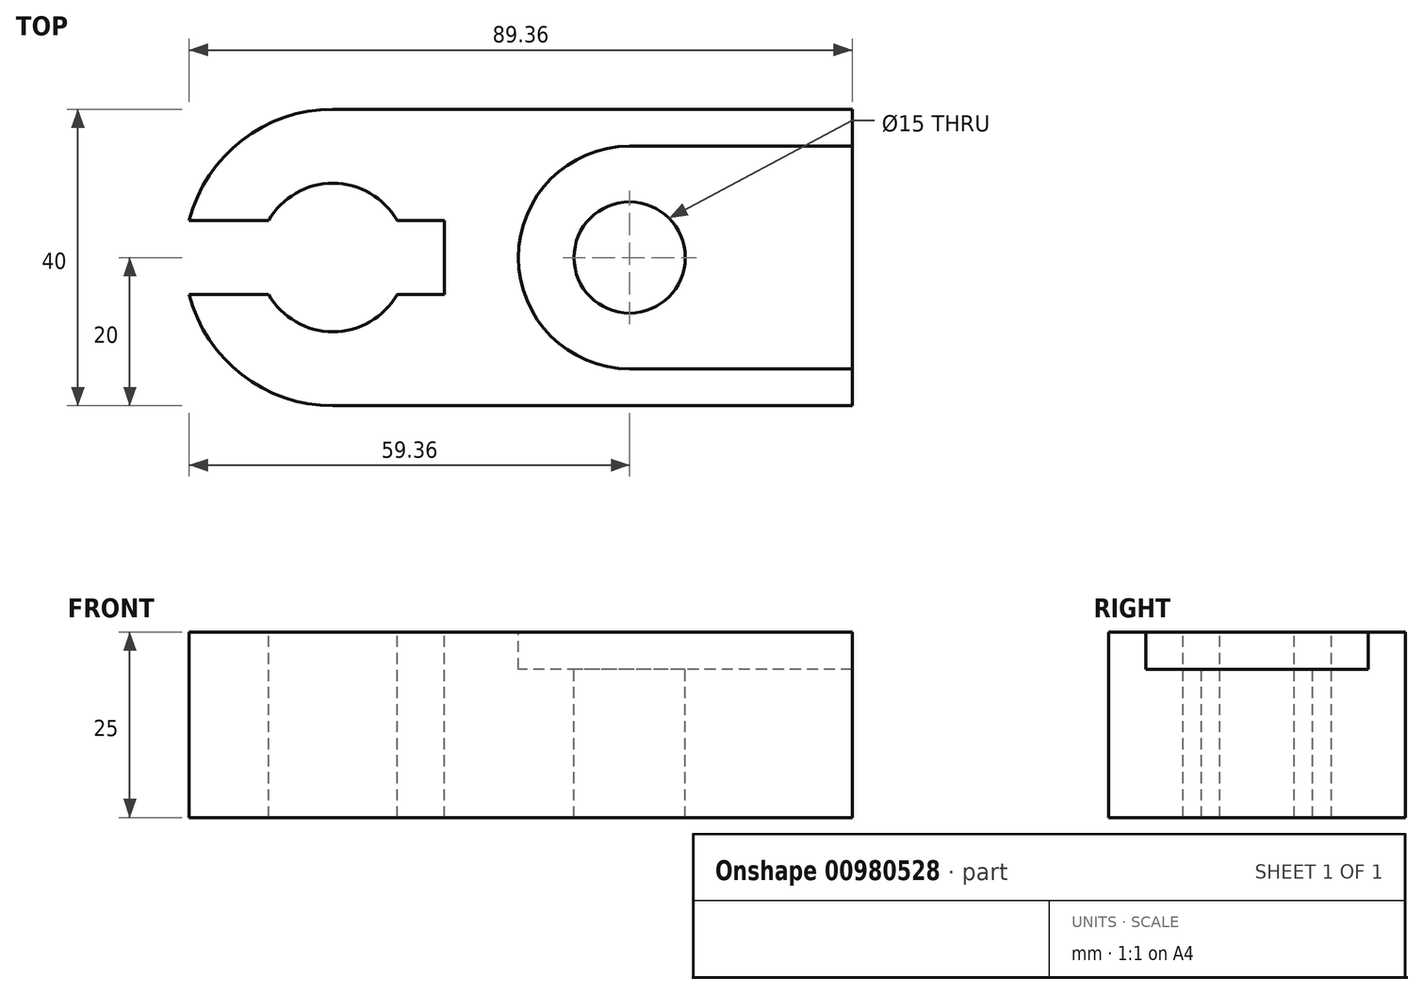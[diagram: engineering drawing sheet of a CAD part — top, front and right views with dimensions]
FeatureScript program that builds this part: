
annotation { "Feature Type Name" : "Feature", "Feature Type Description" : "" }
export const myFeature = defineFeature(function(context is Context, id is Id, definition is map)
    precondition{}
    {
        {
            var Q0;
            Q0=qCreatedBy(makeId("Top.planeOp"),FACE);
            var sketch = newSketch(context, id + "F0", { "sketchPlane" : qUnion([Q0])});
            skLineSegment(sketch, "E0.bottom", {"start": v(45, 20) * mm, "end": v(-25, 20) * mm});
            skLineSegment(sketch, "E0.top", {"start": v(45, -20) * mm, "end": v(-25, -20) * mm});
            skLineSegment(sketch, "E0.left", {"start": v(45, 20) * mm, "end": v(45, -20) * mm});
            skLineSegment(sketch, "E0.right", {"start": v(-45, 0) * mm, "end": v(-45, 0) * mm});
            skPoint(sketch, "E0.middle", {"position": v(0, 0) * mm});
            skPoint(sketch, "E1.visualSharp", {"position": v(-45, 20) * mm});
            skArc(sketch, "E1.filletArc", {"start": v(-25, 20) * mm, "mid": v(-39.14, 14.14) * mm, "end": v(-45, 0) * mm});
            skPoint(sketch, "E2.visualSharp", {"position": v(-45, -20) * mm});
            skArc(sketch, "E2.filletArc", {"start": v(-45, 0) * mm, "mid": v(-39.14, -14.14) * mm, "end": v(-25, -20) * mm});
            skSolve(sketch);
        }
        {
            var Q0;
            Q0=makeQuery(id+"F0.imprint","IMPRINT",FACE,{"disambiguationData":[TD([[makeQuery(id+"F0.imprint","IMPRINT",EDGE,{"derivedFrom":sQuery(id+"F0.wireOp",EDGE,"E0.bottom")}),1.0]])]});
            extrude(context, id + "F1", {"entities" : qUnion([Q0]), "depth" : 25 * mm, "offsetDistance" : 25 * mm});
        }
        {
            var Q0;
            Q0=makeQuery(id+"F1.opExtrude","CAP_FACE",FACE,{"disambiguationData":[OSD([sQuery(id+"F0.wireOp",EDGE,"E0.bottom"),sQuery(id+"F0.wireOp",EDGE,"E0.top"),sQuery(id+"F0.wireOp",EDGE,"E0.left"),sQuery(id+"F0.wireOp",EDGE,"E1.filletArc"),sQuery(id+"F0.wireOp",EDGE,"E2.filletArc")])],"isStart":false});
            var sketch = newSketch(context, id + "F2", { "sketchPlane" : qUnion([Q0])});
            skArc(sketch, "E3", {"start": v(-33.66, -5) * mm, "mid": v(-25, -10) * mm, "end": v(-16.34, -5) * mm});
            skLineSegment(sketch, "E4.bottom", {"start": v(-51, 5) * mm, "end": v(-33.66, 5) * mm});
            skLineSegment(sketch, "E4.top", {"start": v(-51, -5) * mm, "end": v(-33.66, -5) * mm});
            skLineSegment(sketch, "E4.right", {"start": v(-10, 5) * mm, "end": v(-10, -5) * mm});
            skLineSegment(sketch, "E5.trimOffspring", {"start": v(-16.34, -5) * mm, "end": v(-10, -5) * mm});
            skLineSegment(sketch, "E6.trimOffspring", {"start": v(-16.34, 5) * mm, "end": v(-10, 5) * mm});
            skArc(sketch, "E7.trimOffspring", {"start": v(-16.34, 5) * mm, "mid": v(-25, 10) * mm, "end": v(-33.66, 5) * mm});
            skLineSegment(sketch, "E8", {"start": v(-51, -5) * mm, "end": v(-51, 5) * mm});
            skPoint(sketch, "E9.orphan", {"position": v(-40, -5) * mm});
            skPoint(sketch, "E10.orphan", {"position": v(-40, 5) * mm});
            skSolve(sketch);
        }
        {
            var Q0;
            {var subQ1=sQuery(id+"F2.wireOp",EDGE,"E3");Q0=makeQuery(id+"F2.imprint","IMPRINT",FACE,{"disambiguationData":[TD([[makeQuery(id+"F2.imprint","IMPRINT",EDGE,{"derivedFrom":subQ1}),1.0]])]});}
            extrude(context, id + "F3", {"entities" : qUnion([Q0]), "operationType" : NewBodyOperationType.REMOVE, "endBound" : BoundingType.UP_TO_NEXT, "oppositeDirection" : true, "depth" : 25 * mm, "offsetDistance" : 25 * mm});
        }
        {
            var Q0;
            Q0=makeQuery(id+"F1.opExtrude","CAP_FACE",FACE,{"disambiguationData":[OSD([sQuery(id+"F0.wireOp",EDGE,"E0.bottom"),sQuery(id+"F0.wireOp",EDGE,"E0.top"),sQuery(id+"F0.wireOp",EDGE,"E0.left"),sQuery(id+"F0.wireOp",EDGE,"E1.filletArc"),sQuery(id+"F0.wireOp",EDGE,"E2.filletArc")])],"isStart":false});
            var sketch = newSketch(context, id + "F4", { "sketchPlane" : qUnion([Q0])});
            skLineSegment(sketch, "E11.bottom", {"start": v(45, 15) * mm, "end": v(15, 15) * mm});
            skLineSegment(sketch, "E11.top", {"start": v(45, -15) * mm, "end": v(15, -15) * mm});
            skLineSegment(sketch, "E11.left", {"start": v(45, 15) * mm, "end": v(45, -15) * mm});
            skLineSegment(sketch, "E11.right", {"start": v(0, 0) * mm, "end": v(0, 0) * mm});
            skPoint(sketch, "E12.visualSharp", {"position": v(0, 15) * mm});
            skArc(sketch, "E12.filletArc", {"start": v(15, 15) * mm, "mid": v(4.4, 10.6) * mm, "end": v(0, 0) * mm});
            skPoint(sketch, "E13.visualSharp", {"position": v(0, -15) * mm});
            skArc(sketch, "E13.filletArc", {"start": v(0, 0) * mm, "mid": v(4.4, -10.6) * mm, "end": v(15, -15) * mm});
            skSolve(sketch);
        }
        {
            var Q0;
            Q0=makeQuery(id+"F4.imprint","IMPRINT",FACE,{"disambiguationData":[TD([[makeQuery(id+"F4.imprint","IMPRINT",EDGE,{"derivedFrom":sQuery(id+"F4.wireOp",EDGE,"E11.bottom")}),1.0]])]});
            extrude(context, id + "F5", {"entities" : qUnion([Q0]), "operationType" : NewBodyOperationType.REMOVE, "oppositeDirection" : true, "depth" : 5 * mm, "offsetDistance" : 25 * mm});
        }
        {
            var Q0;
            Q0=makeQuery(id+"F5.boolean.opBoolean","COPY",FACE,{"derivedFrom":makeQuery(id+"F5.opExtrude","CAP_FACE",FACE,{"disambiguationData":[OSD([sQuery(id+"F4.wireOp",EDGE,"E11.bottom"),sQuery(id+"F4.wireOp",EDGE,"E11.top"),sQuery(id+"F4.wireOp",EDGE,"E11.left"),sQuery(id+"F4.wireOp",EDGE,"E12.filletArc"),sQuery(id+"F4.wireOp",EDGE,"E13.filletArc")])],"isStart":false})});
            var sketch = newSketch(context, id + "F6", { "sketchPlane" : qUnion([Q0])});
            skCircle(sketch, "E14", {"center": v(15, 0) * mm, "radius": 7.5 * mm});
            skSolve(sketch);
        }
        {
            var Q0;
            Q0=makeQuery(id+"F6.imprint","IMPRINT",FACE,{"disambiguationData":[TD([[makeQuery(id+"F6.imprint","IMPRINT",EDGE,{"derivedFrom":sQuery(id+"F6.wireOp",EDGE,"E14")}),1.0]])]});
            extrude(context, id + "F7", {"entities" : qUnion([Q0]), "operationType" : NewBodyOperationType.REMOVE, "endBound" : BoundingType.UP_TO_NEXT, "oppositeDirection" : true, "depth" : 25 * mm, "offsetDistance" : 25 * mm});
        }
    });
